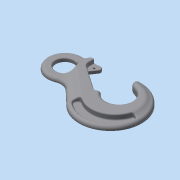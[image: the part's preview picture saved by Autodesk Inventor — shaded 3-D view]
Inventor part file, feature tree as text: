
AUTODESK INVENTOR PART (.ipt)
format: ipt  version: 2017 (Build 210142000, 142)  size: 864,768 bytes
history: native  units: mm
features: fillet x18, sketch x14, extrude x8, revolve x6, plane x4, other x2, mirror x2
ambient origin geometry x8: Origin, YZ Plane, XZ Plane, XY Plane, X Axis, Y Axis, Z Axis, Center Point
bodies: Solid1 (feature_tree)
feature tree (54):
  extrude  "Extrusion1"  [1 undecoded]
  plane  "Work Plane1"
  other  "Work Axis1"
  revolve  "Revolution1"  [1 undecoded]
  revolve  "Revolution2"  [1 undecoded]
  extrude  "Extrusion2"  Depth=45.378561mm
  other  "Work Axis2"
  revolve  "Revolution3"  [1 undecoded]
  extrude  "Extrusion3"  Depth=10.0mm
  extrude  "Extrusion4"  Depth=20.0mm TaperAngle=0.0deg
  revolve  "Revolution4"  [1 undecoded]
  revolve  "Revolution5"  [1 undecoded]
  extrude  "Extrusion5"  Depth=45.378561mm
  revolve  "Revolution6"  [1 undecoded]
  fillet  "Fillet9"  Radius=10.0mm
  fillet  "Fillet10"  Radius=5.0mm
  fillet  "Fillet11"  Radius=3.0mm
  fillet  "Fillet12"  Radius=5.0mm
  mirror  "Mirror8"
  extrude  "Extrusion6"  Depth=20.0mm TaperAngle=0.0deg
  fillet  "Fillet13"  Radius=2.0mm
  fillet  "Fillet14"  Radius=2.0mm
  fillet  "Fillet15"  Radius=2.0mm
  fillet  "Fillet16"  Radius=2.0mm
  fillet  "Fillet17"  Radius=2.0mm
  fillet  "Fillet18"  Radius=2.0mm
  fillet  "Fillet19"  Radius=2.0mm
  fillet  "Fillet20"  Radius=2.0mm
  fillet  "Fillet21"  Radius=1.0mm
  fillet  "Fillet22"  Radius=1.0mm
  fillet  "Fillet23"  Radius=1.0mm
  fillet  "Fillet24"  Radius=1.0mm
  plane  "Work Plane2"
  extrude  "Extrusion7"  Depth=10.0mm
  mirror  "Mirror9"
  fillet  "Fillet32"  Radius=3.0mm
  fillet  "Fillet33"  Radius=10.0mm
  plane  "Work Plane3"
  plane  "Work Plane4"
  extrude  "Extrusion8"  Depth=2.0mm
  sketch  "Sketch1"  dims[d0=24.6mm d1=0.0mm d2=-10.0mm]
  sketch  "Sketch2"  dims[d3=25.0mm d4=62.3mm]
  sketch  "Sketch3"  dims[d5=34.906585mm d6=6.981317mm]
  sketch  "Sketch4"  dims[d7=150.0mm d8=0.0mm d9=45.378561mm]
  sketch  "Sketch5"  dims[d10=15.0mm d12=5.0mm]
  sketch  "Sketch6"  dims[d14=2.0mm d15=10.0mm]
  sketch  "Sketch7"  dims[d16=7.0mm d17=0.0mm d18=20.0mm d19=0.0mm]
  sketch  "Sketch8"  dims[d28=25.0mm d29=62.3mm]
  sketch  "Sketch9"  dims[d30=34.906585mm d31=6.981317mm]
  sketch  "Sketch10"  dims[d32=140.0mm d33=0.0mm d34=45.378561mm]
  sketch  "Sketch11"  dims[d35=10.0mm d36=5.0mm d37=10.0mm d38=5.0mm d39=3.0mm d40=5.0mm]
  sketch  "Sketch12"  dims[d41=10.0mm d42=20.0mm d43=0.0mm d44=2.0mm d45=2.0mm d46=2.0mm d47=2.0mm d48=2.0mm d49=2.0mm d50=2.0mm d51=2.0mm d52=1.0mm d53=1.0mm d54=1.0mm d55=1.0mm]
  sketch  "Sketch13"  dims[d56=3.0mm d57=5.0mm d58=3.0mm d59=10.0mm d60=0.0mm]
  sketch  "Sketch14"  dims[d68=2.0mm d69=2.0mm d70=300.0mm d71=0.0mm]
note: 7 required parameter values undecoded (feature->parameter linkage not recoverable at this tier; creation-order binding heuristic only, values carry confidence <= 0.55)